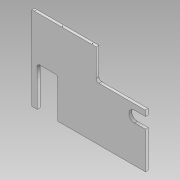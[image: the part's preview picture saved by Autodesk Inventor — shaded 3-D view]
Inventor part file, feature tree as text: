
AUTODESK INVENTOR PART (.ipt)
format: ipt  version: 2021.4 (Build 254397000, 397)  size: 149,504 bytes
history: native  units: in
note: dims shown in document units (in); Inventor stores cm internally (conversion verified against a paired STEP export)
features: sketch x4, extrude x2, hole x2
ambient origin geometry x8: Origin, YZ Plane, XZ Plane, XY Plane, X Axis, Y Axis, Z Axis, Center Point
bodies: Solid1 (feature_tree)
feature tree (8):
  extrude  "Extrusion1"  Depth=12.0079in
  extrude  "Extrusion2"  Depth=5.7087in
  sketch  "Sketch3"  dims[d5=2.9528in d6=0.7874in]
  sketch  "Sketch4"  dims[d7=1.5748in d8=1.5748in d9=5.1181in d10=4.3307in d11=7.0866in d12=0.3937in d13=0.0in d14=0.2362in d15=16.3386in d16=0.7874in d17=0.315in d18=3.937in d19=5.9055in d20=4.7244in d22=0.2362in d23=0.315in d24=8.2677in d25=3.937in d26=0.0968in d27=0.2362in d28=0.1476in d29=0.0984in d30=90.0deg d31=0.3937in d32=0.0in d33=0.0968in d34=0.2362in d35=0.1476in d36=0.0984in d37=90.0deg d38=0.3937in d39=0.0in d41=0.3937in]
  hole  "Hole1"  [1 undecoded]
  hole  "Hole2"  [1 undecoded]
  sketch  "Sketch1"  dims[d0=16.3386in d1=12.0079in]
  sketch  "Sketch2"  dims[d2=0.3937in d3=0.0in d4=5.7087in]
note: 2 required parameter values undecoded (feature->parameter linkage not recoverable at this tier; creation-order binding heuristic only, values carry confidence <= 0.55)
